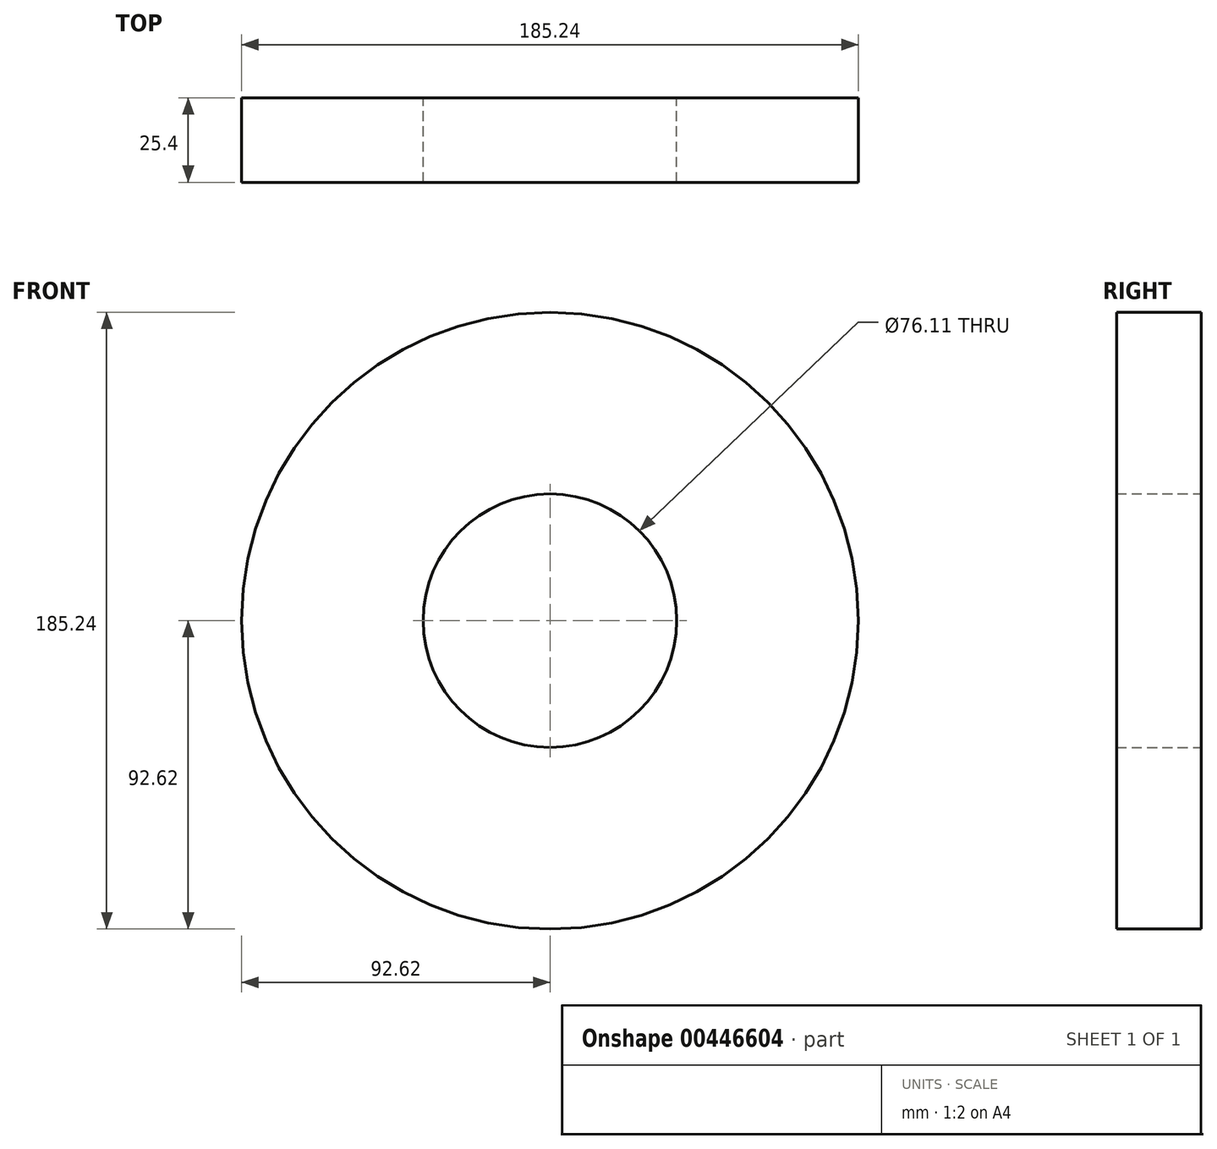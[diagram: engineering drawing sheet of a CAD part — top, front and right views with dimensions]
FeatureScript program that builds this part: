
annotation { "Feature Type Name" : "Feature", "Feature Type Description" : "" }
export const myFeature = defineFeature(function(context is Context, id is Id, definition is map)
    precondition{}
    {
        {
            var Q0;
            Q0=qCreatedBy(makeId("Front.planeOp"),FACE);
            var sketch = newSketch(context, id + "F0", { "sketchPlane" : qUnion([Q0])});
            skCircle(sketch, "E0", {"center": v(0, 0) * mm, "radius": 92.62 * mm});
            skCircle(sketch, "E1", {"center": v(0, 0) * mm, "radius": 38.05 * mm});
            skSolve(sketch);
        }
        {
            var Q0;
            Q0 = qSketchRegion(id + "F0", true);
            extrude(context, id + "F1", {"entities" : qUnion([Q0]), "depth" : 25.4 * mm});
        }
    });
